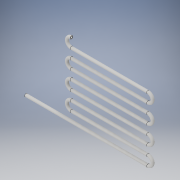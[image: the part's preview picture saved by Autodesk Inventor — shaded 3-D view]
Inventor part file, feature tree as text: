
AUTODESK INVENTOR PART (.ipt)
format: ipt  version: 2019.4 (Build 234330000, 330)  size: 231,936 bytes
history: native  units: mm
features: sketch x4, other x3, sweep x1, pattern_linear x1, extrude x1
ambient origin geometry x8: Origin, YZ Plane, XZ Plane, XY Plane, X Axis, Y Axis, Z Axis, Center Point
bodies: Body1 (feature_tree)
feature tree (10):
  other  "Sólido1"
  sketch  "Esboço3"  dims[d21=50.0mm d23=50.0mm]
  other  "Plano de trabalho3"
  sweep  "Varredura1"
  pattern_linear  "Padrão retangular1"  Count1=5  [1 undecoded]
  sketch  "Esboço 3D1"  dims[d18=1000.0mm d19=1000.0mm d20=50.0mm]
  extrude  "Extrusão1"  Depth=50.0mm
  sketch  "Esboço5"  dims[d24=80.0mm]
  sketch  "Esboço6"  dims[d25=80.0mm d26=40.0mm d28=200.0mm d29=10.0mm d31=10.0mm d33=80.0mm d36=19.05mm d37=6.0mm d38=0.0mm d39=0.0mm d40=40.0mm d42=200.0mm d43=500.0mm d44=0.0mm]
  other  "Contorno projetado1"
note: 1 required parameter value undecoded (feature->parameter linkage not recoverable at this tier; creation-order binding heuristic only, values carry confidence <= 0.55)
